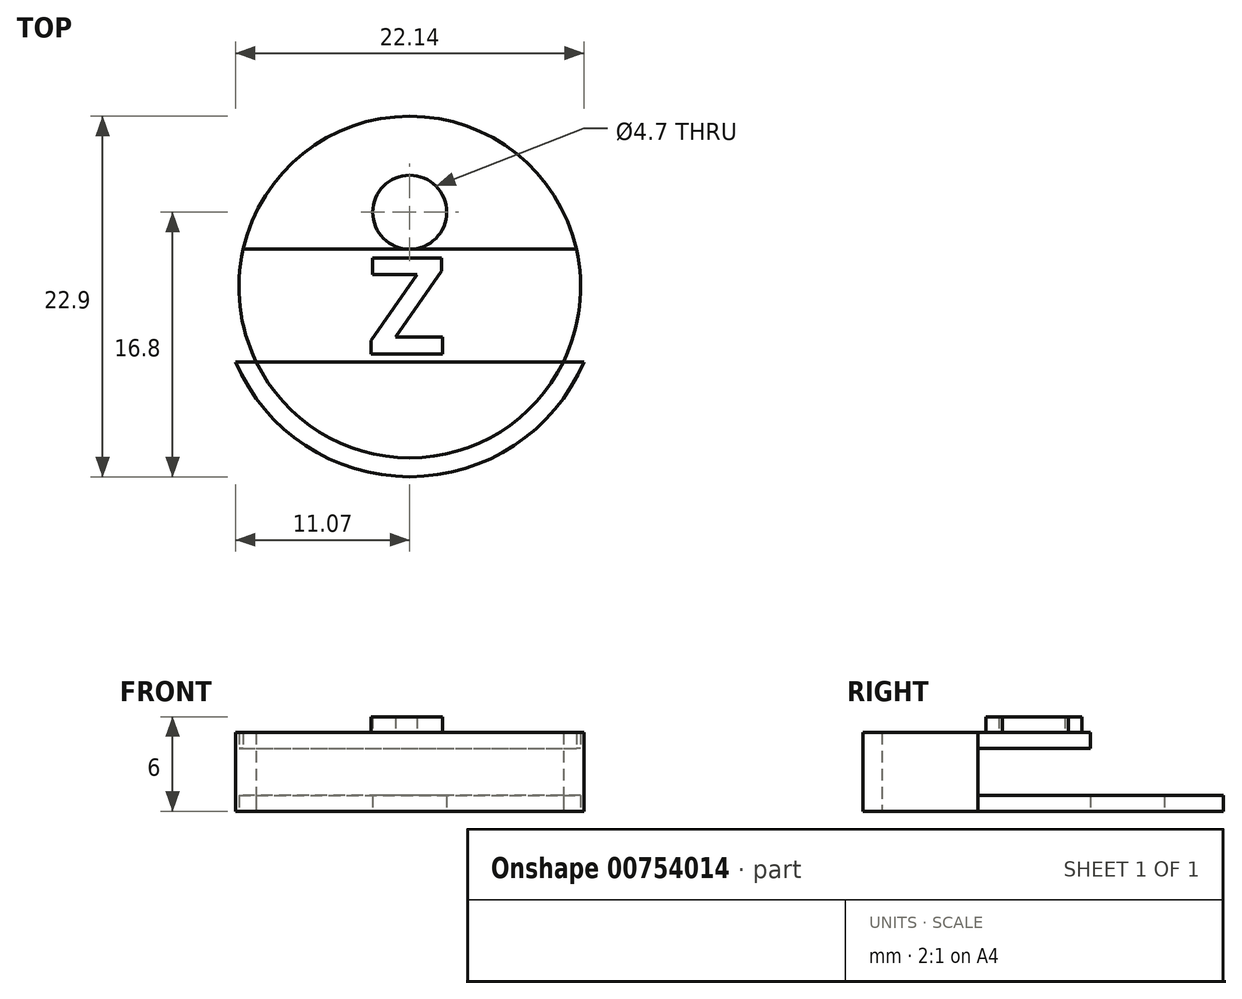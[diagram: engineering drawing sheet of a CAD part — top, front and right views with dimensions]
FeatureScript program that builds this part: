
annotation { "Feature Type Name" : "Feature", "Feature Type Description" : "" }
export const myFeature = defineFeature(function(context is Context, id is Id, definition is map)
    precondition{}
    {
        {
            var Q0;
            Q0=qCreatedBy(makeId("Top.planeOp"),FACE);
            var sketch = newSketch(context, id + "F0", { "sketchPlane" : qUnion([Q0])});
            skCircle(sketch, "E0", {"center": v(0, 0) * mm, "radius": 12.05 * mm});
            skLineSegment(sketch, "E1", {"start": v(-11.07, -4.75) * mm, "end": v(11.07, -4.75) * mm});
            skCircle(sketch, "E2", {"center": v(0, 4.75) * mm, "radius": 2.35 * mm});
            skCircle(sketch, "E3", {"center": v(0, 0) * mm, "radius": 10.85 * mm});
            skLineSegment(sketch, "E4", {"start": v(0, 2.4) * mm, "end": v(-10.58, 2.4) * mm});
            skLineSegment(sketch, "E5", {"start": v(0, 2.4) * mm, "end": v(10.58, 2.4) * mm});
            skText(sketch, "E6", { "text": "Z", "fontName": "OpenSans-Bold.ttf"});
            const initialGuessF0  = {"E6": [-0.00265, -0.00425, 1, 0, 0.00615]};
            skSetInitialGuess(sketch, initialGuessF0);
            skSolve(sketch);
        }
        {
            var Q0;
            {var subQ0=sQuery(id+"F0.wireOp",EDGE,"E4");Q0=makeQuery(id+"F0.imprint","IMPRINT",FACE,{"disambiguationData":[TD([[makeQuery(id+"F0.imprint","IMPRINT",EDGE,{"derivedFrom":subQ0}),1.0]])]});}
            var Q1;
            {var subQ0=sQuery(id+"F0.wireOp",EDGE,"E1");var subQ1=sQuery(id+"F0.wireOp",EDGE,"E0");var subQ5=makeQuery(id+"F0.imprint","INTERSECT",VERTEX,{"disambiguationData":[OD(0.0)],"derivedFrom":[subQ1,subQ0]});Q1=makeQuery(id+"F0.imprint","IMPRINT",FACE,{"disambiguationData":[TD([[makeQuery(id+"F0.imprint","IMPRINT",EDGE,{"disambiguationData":[TD([[subQ5,1.0]])],"derivedFrom":subQ1}),1.0]])]});}
            var Q2;
            Q2=makeQuery(id+"F0.imprint","IMPRINT",FACE,{"disambiguationData":[TD([[makeQuery(id+"F0.imprint","IMPRINT",EDGE,{"derivedFrom":sQuery(id+"F0.wireOp",EDGE,"3db4fb92-41e3-4f33-b393-5101edaef4c4.sketch_text.stroke-59")}),1.0]])]});
            var Q3;
            {var subQ0=sQuery(id+"F0.wireOp",EDGE,"3db4fb92-41e3-4f33-b393-5101edaef4c4.sketch_text.stroke-5");Q3=makeQuery(id+"F0.imprint","IMPRINT",FACE,{"disambiguationData":[TD([[makeQuery(id+"F0.imprint","IMPRINT",EDGE,{"derivedFrom":subQ0}),1.0]])]});}
            extrude(context, id + "F1", {"entities" : qUnion([Q0, Q1, Q2, Q3]), "depth" : 5 * mm, "offsetDistance" : 25 * mm});
        }
        {
            var Q0;
            Q0=makeQuery(id+"F0.imprint","IMPRINT",FACE,{"disambiguationData":[TD([[makeQuery(id+"F0.imprint","IMPRINT",EDGE,{"derivedFrom":sQuery(id+"F0.wireOp",EDGE,"E6.sketch_text.stroke-0")}),-1.0]])]});
            extrude(context, id + "F2", {"entities" : qUnion([Q0]), "operationType" : NewBodyOperationType.ADD, "depth" : 6 * mm, "offsetDistance" : 25 * mm});
        }
        {
            var Q0;
            {var subQ0=sQuery(id+"F0.wireOp",EDGE,"E4");Q0=makeQuery(id+"F0.imprint","IMPRINT",FACE,{"disambiguationData":[TD([[makeQuery(id+"F0.imprint","IMPRINT",EDGE,{"derivedFrom":subQ0}),1.0]])]});}
            var Q1;
            Q1=makeQuery(id+"F0.imprint","IMPRINT",FACE,{"disambiguationData":[TD([[makeQuery(id+"F0.imprint","IMPRINT",EDGE,{"derivedFrom":sQuery(id+"F0.wireOp",EDGE,"3db4fb92-41e3-4f33-b393-5101edaef4c4.sketch_text.stroke-0")}),-1.0]])]});
            var Q2;
            Q2=makeQuery(id+"F0.imprint","IMPRINT",FACE,{"disambiguationData":[TD([[makeQuery(id+"F0.imprint","IMPRINT",EDGE,{"derivedFrom":sQuery(id+"F0.wireOp",EDGE,"3db4fb92-41e3-4f33-b393-5101edaef4c4.sketch_text.stroke-28")}),-1.0]])]});
            var Q3;
            Q3=makeQuery(id+"F0.imprint","IMPRINT",FACE,{"disambiguationData":[TD([[makeQuery(id+"F0.imprint","IMPRINT",EDGE,{"derivedFrom":sQuery(id+"F0.wireOp",EDGE,"3db4fb92-41e3-4f33-b393-5101edaef4c4.sketch_text.stroke-41")}),-1.0]])]});
            var Q4;
            Q4=makeQuery(id+"F0.imprint","IMPRINT",FACE,{"disambiguationData":[TD([[makeQuery(id+"F0.imprint","IMPRINT",EDGE,{"derivedFrom":sQuery(id+"F0.wireOp",EDGE,"3db4fb92-41e3-4f33-b393-5101edaef4c4.sketch_text.stroke-47")}),-1.0]])]});
            var Q5;
            Q5=makeQuery(id+"F0.imprint","IMPRINT",FACE,{"disambiguationData":[TD([[makeQuery(id+"F0.imprint","IMPRINT",EDGE,{"derivedFrom":sQuery(id+"F0.wireOp",EDGE,"3db4fb92-41e3-4f33-b393-5101edaef4c4.sketch_text.stroke-59")}),-1.0]])]});
            var Q6;
            Q6=makeQuery(id+"F0.imprint","IMPRINT",FACE,{"disambiguationData":[TD([[makeQuery(id+"F0.imprint","IMPRINT",EDGE,{"derivedFrom":sQuery(id+"F0.wireOp",EDGE,"3db4fb92-41e3-4f33-b393-5101edaef4c4.sketch_text.stroke-59")}),1.0]])]});
            var Q7;
            {var subQ0=sQuery(id+"F0.wireOp",EDGE,"3db4fb92-41e3-4f33-b393-5101edaef4c4.sketch_text.stroke-5");Q7=makeQuery(id+"F0.imprint","IMPRINT",FACE,{"disambiguationData":[TD([[makeQuery(id+"F0.imprint","IMPRINT",EDGE,{"derivedFrom":subQ0}),1.0]])]});}
            var Q8;
            Q8=makeQuery(id+"F0.imprint","IMPRINT",FACE,{"disambiguationData":[TD([[makeQuery(id+"F0.imprint","IMPRINT",EDGE,{"derivedFrom":sQuery(id+"F0.wireOp",EDGE,"E6.sketch_text.stroke-0")}),-1.0]])]});
            extrude(context, id + "F3", {"entities" : qUnion([Q0, Q1, Q2, Q3, Q4, Q5, Q6, Q7, Q8]), "operationType" : NewBodyOperationType.REMOVE, "depth" : 4 * mm, "offsetDistance" : 25 * mm});
        }
        {
            var Q0;
            Q0=makeQuery(id+"F0.imprint","IMPRINT",FACE,{"disambiguationData":[TD([[makeQuery(id+"F0.imprint","IMPRINT",EDGE,{"derivedFrom":sQuery(id+"F0.wireOp",EDGE,"E2")}),-1.0]])]});
            var Q1;
            {var subQ0=sQuery(id+"F0.wireOp",EDGE,"E4");Q1=makeQuery(id+"F0.imprint","IMPRINT",FACE,{"disambiguationData":[TD([[makeQuery(id+"F0.imprint","IMPRINT",EDGE,{"derivedFrom":subQ0}),1.0]])]});}
            var Q2;
            Q2=makeQuery(id+"F0.imprint","IMPRINT",FACE,{"disambiguationData":[TD([[makeQuery(id+"F0.imprint","IMPRINT",EDGE,{"derivedFrom":sQuery(id+"F0.wireOp",EDGE,"3db4fb92-41e3-4f33-b393-5101edaef4c4.sketch_text.stroke-0")}),-1.0]])]});
            var Q3;
            Q3=makeQuery(id+"F0.imprint","IMPRINT",FACE,{"disambiguationData":[TD([[makeQuery(id+"F0.imprint","IMPRINT",EDGE,{"derivedFrom":sQuery(id+"F0.wireOp",EDGE,"3db4fb92-41e3-4f33-b393-5101edaef4c4.sketch_text.stroke-28")}),-1.0]])]});
            var Q4;
            Q4=makeQuery(id+"F0.imprint","IMPRINT",FACE,{"disambiguationData":[TD([[makeQuery(id+"F0.imprint","IMPRINT",EDGE,{"derivedFrom":sQuery(id+"F0.wireOp",EDGE,"3db4fb92-41e3-4f33-b393-5101edaef4c4.sketch_text.stroke-41")}),-1.0]])]});
            var Q5;
            Q5=makeQuery(id+"F0.imprint","IMPRINT",FACE,{"disambiguationData":[TD([[makeQuery(id+"F0.imprint","IMPRINT",EDGE,{"derivedFrom":sQuery(id+"F0.wireOp",EDGE,"3db4fb92-41e3-4f33-b393-5101edaef4c4.sketch_text.stroke-47")}),-1.0]])]});
            var Q6;
            Q6=makeQuery(id+"F0.imprint","IMPRINT",FACE,{"disambiguationData":[TD([[makeQuery(id+"F0.imprint","IMPRINT",EDGE,{"derivedFrom":sQuery(id+"F0.wireOp",EDGE,"3db4fb92-41e3-4f33-b393-5101edaef4c4.sketch_text.stroke-59")}),-1.0]])]});
            var Q7;
            Q7=makeQuery(id+"F0.imprint","IMPRINT",FACE,{"disambiguationData":[TD([[makeQuery(id+"F0.imprint","IMPRINT",EDGE,{"derivedFrom":sQuery(id+"F0.wireOp",EDGE,"3db4fb92-41e3-4f33-b393-5101edaef4c4.sketch_text.stroke-59")}),1.0]])]});
            var Q8;
            {var subQ0=sQuery(id+"F0.wireOp",EDGE,"3db4fb92-41e3-4f33-b393-5101edaef4c4.sketch_text.stroke-5");Q8=makeQuery(id+"F0.imprint","IMPRINT",FACE,{"disambiguationData":[TD([[makeQuery(id+"F0.imprint","IMPRINT",EDGE,{"derivedFrom":subQ0}),1.0]])]});}
            var Q9;
            Q9=makeQuery(id+"F0.imprint","IMPRINT",FACE,{"disambiguationData":[TD([[makeQuery(id+"F0.imprint","IMPRINT",EDGE,{"derivedFrom":sQuery(id+"F0.wireOp",EDGE,"E6.sketch_text.stroke-0")}),-1.0]])]});
            extrude(context, id + "F4", {"entities" : qUnion([Q0, Q1, Q2, Q3, Q4, Q5, Q6, Q7, Q8, Q9]), "operationType" : NewBodyOperationType.ADD, "depth" : 1 * mm, "offsetDistance" : 25 * mm});
        }
    });
